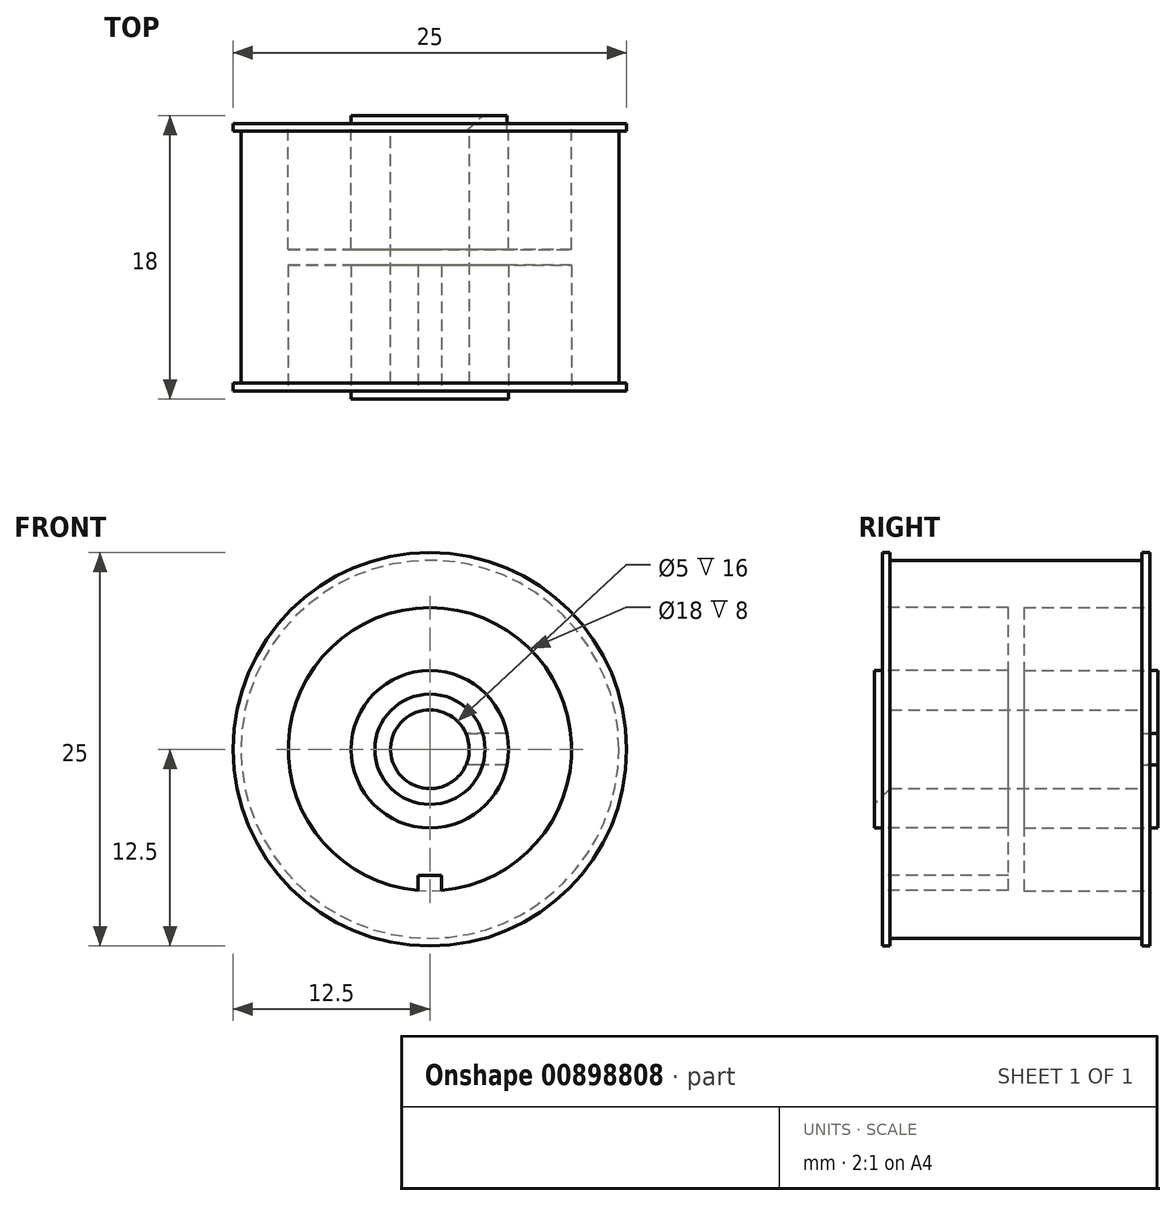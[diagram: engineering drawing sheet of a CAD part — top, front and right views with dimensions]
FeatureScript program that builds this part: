
annotation { "Feature Type Name" : "Feature", "Feature Type Description" : "" }
export const myFeature = defineFeature(function(context is Context, id is Id, definition is map)
    precondition{}
    {
        {
            var Q0;
            Q0=qCreatedBy(makeId("Front.planeOp"),FACE);
            var sketch = newSketch(context, id + "F0", { "sketchPlane" : qUnion([Q0])});
            skCircle(sketch, "E0", {"center": v(0, 0) * mm, "radius": 12.5 * mm});
            skSolve(sketch);
        }
        {
            var Q0;
            Q0 = qSketchRegion(id + "F0", true);
            extrude(context, id + "F1", {"entities" : qUnion([Q0]), "depth" : 17 * mm, "offsetDistance" : 25 * mm});
        }
        {
            var Q0;
            Q0=qCreatedBy(makeId("Top.planeOp"),FACE);
            var sketch = newSketch(context, id + "F2", { "sketchPlane" : qUnion([Q0])});
            skLineSegment(sketch, "E1.bottom", {"start": v(-13.5, -0.5) * mm, "end": v(-12, -0.5) * mm});
            skLineSegment(sketch, "E1.top", {"start": v(-13.5, -16.5) * mm, "end": v(-12, -16.5) * mm});
            skLineSegment(sketch, "E1.left", {"start": v(-13.5, -0.5) * mm, "end": v(-13.5, -16.5) * mm});
            skLineSegment(sketch, "E1.right", {"start": v(-12, -0.5) * mm, "end": v(-12, -16.5) * mm});
            skLineSegment(sketch, "E2", {"start": v(0, 0.56) * mm, "end": v(0, -16.99) * mm});
            skSolve(sketch);
        }
        {
            var Q0;
            Q0 = qSketchRegion(id + "F2", true);
            var Q1;
            Q1=sQuery(id+"F2.wireOp",EDGE,"E2");
            revolve(context, id + "F3", {"operationType" : NewBodyOperationType.REMOVE, "surfaceOperationType" : NewSurfaceOperationType.NEW, "entities" : qUnion([Q0]), "axis" : qUnion([Q1]), "revolveType" : RevolveType.FULL, "oppositeDirection" : true});
        }
        {
            var Q0;
            Q0=makeQuery(id+"F1.opExtrude","CAP_FACE",FACE,{"disambiguationData":[OSD([sQuery(id+"F0.wireOp",EDGE,"E0")])],"isStart":true});
            var sketch = newSketch(context, id + "F4", { "sketchPlane" : qUnion([Q0])});
            skCircle(sketch, "E3", {"center": v(0, 0) * mm, "radius": 2.5 * mm});
            skSolve(sketch);
        }
        {
            var Q0;
            Q0 = qSketchRegion(id + "F4", true);
            extrude(context, id + "F5", {"entities" : qUnion([Q0]), "operationType" : NewBodyOperationType.REMOVE, "endBound" : BoundingType.THROUGH_ALL, "oppositeDirection" : true, "depth" : 25 * mm, "offsetDistance" : 25 * mm});
        }
        {
            var Q0;
            Q0=makeQuery(id+"F1.opExtrude","CAP_FACE",FACE,{"disambiguationData":[OSD([sQuery(id+"F0.wireOp",EDGE,"E0")])],"isStart":true});
            var sketch = newSketch(context, id + "F6", { "sketchPlane" : qUnion([Q0])});
            skCircle(sketch, "E4", {"center": v(0, 0) * mm, "radius": 9 * mm});
            skCircle(sketch, "E5", {"center": v(0, 0) * mm, "radius": 5 * mm});
            skSolve(sketch);
        }
        {
            var Q0;
            Q0 = qSketchRegion(id + "F6", true);
            extrude(context, id + "F7", {"entities" : qUnion([Q0]), "operationType" : NewBodyOperationType.REMOVE, "oppositeDirection" : true, "depth" : 8 * mm, "offsetDistance" : 25 * mm});
        }
        {
            var Q0;
            Q0=makeQuery(id+"F7.boolean.opBoolean","SPLIT",FACE,{"disambiguationData":[TD([makeQuery(id+"F5.boolean.opBoolean","COPY",FACE,{"derivedFrom":makeQuery(id+"F5.opExtrude","SWEPT_FACE",FACE,{"disambiguationData":[OSD([sQuery(id+"F4.wireOp",EDGE,"E3")])]})})])],"derivedFrom":makeQuery(id+"F1.opExtrude","CAP_FACE",FACE,{"disambiguationData":[OSD([sQuery(id+"F0.wireOp",EDGE,"E0")])],"isStart":true})});
            var sketch = newSketch(context, id + "F8", { "sketchPlane" : qUnion([Q0])});
            skLineSegment(sketch, "E6.bottom", {"start": v(-6.33, 1) * mm, "end": v(-1.4, 1) * mm});
            skLineSegment(sketch, "E6.top", {"start": v(-6.33, -1) * mm, "end": v(-1.4, -1) * mm});
            skLineSegment(sketch, "E6.left", {"start": v(-6.33, 1) * mm, "end": v(-6.33, -1) * mm});
            skLineSegment(sketch, "E6.right", {"start": v(-1.4, 1) * mm, "end": v(-1.4, -1) * mm});
            skSolve(sketch);
        }
        {
            var Q0;
            Q0 = qSketchRegion(id + "F8", true);
            extrude(context, id + "F9", {"entities" : qUnion([Q0]), "operationType" : NewBodyOperationType.REMOVE, "oppositeDirection" : true, "depth" : .5 * mm, "offsetDistance" : 25 * mm});
        }
        {
            var Q0;
            Q0=makeQuery(id+"F1.opExtrude","CAP_FACE",FACE,{"disambiguationData":[OSD([sQuery(id+"F0.wireOp",EDGE,"E0")])],"isStart":false});
            var sketch = newSketch(context, id + "F10", { "sketchPlane" : qUnion([Q0])});
            skArc(sketch, "E7", {"start": v(0.75, -8.97) * mm, "mid": v(0, 9) * mm, "end": v(-0.75, -8.97) * mm});
            skCircle(sketch, "E8", {"center": v(0, 0) * mm, "radius": 5 * mm});
            skLineSegment(sketch, "E9.top", {"start": v(-0.75, -8) * mm, "end": v(0.75, -8) * mm});
            skLineSegment(sketch, "E9.left", {"start": v(-0.75, -8.97) * mm, "end": v(-0.75, -8) * mm});
            skLineSegment(sketch, "E9.right", {"start": v(0.75, -8.97) * mm, "end": v(0.75, -8) * mm});
            skSolve(sketch);
        }
        {
            var Q0;
            Q0 = qSketchRegion(id + "F10", true);
            extrude(context, id + "F11", {"entities" : qUnion([Q0]), "operationType" : NewBodyOperationType.REMOVE, "oppositeDirection" : true, "depth" : 8 * mm, "offsetDistance" : 25 * mm});
        }
        {
            var Q0;
            Q0=makeQuery(id+"F7.boolean.opBoolean","SPLIT",FACE,{"disambiguationData":[TD([makeQuery(id+"F5.boolean.opBoolean","COPY",FACE,{"derivedFrom":makeQuery(id+"F5.opExtrude","SWEPT_FACE",FACE,{"disambiguationData":[OSD([sQuery(id+"F4.wireOp",EDGE,"E3")])]})})])],"derivedFrom":makeQuery(id+"F1.opExtrude","CAP_FACE",FACE,{"disambiguationData":[OSD([sQuery(id+"F0.wireOp",EDGE,"E0")])],"isStart":true})});
            extrude(context, id + "F12", {"entities" : qUnion([Q0]), "operationType" : NewBodyOperationType.ADD, "depth" : .5 * mm, "offsetDistance" : 25 * mm});
        }
        {
            var Q0;
            Q0=makeQuery(id+"F11.boolean.opBoolean","SPLIT",FACE,{"disambiguationData":[TD([makeQuery(id+"F5.boolean.opBoolean","COPY",FACE,{"derivedFrom":makeQuery(id+"F5.opExtrude","SWEPT_FACE",FACE,{"disambiguationData":[OSD([sQuery(id+"F4.wireOp",EDGE,"E3")])]})})])],"derivedFrom":makeQuery(id+"F1.opExtrude","CAP_FACE",FACE,{"disambiguationData":[OSD([sQuery(id+"F0.wireOp",EDGE,"E0")])],"isStart":false})});
            extrude(context, id + "F13", {"entities" : qUnion([Q0]), "operationType" : NewBodyOperationType.ADD, "depth" : .5 * mm, "offsetDistance" : 25 * mm});
        }
        {
            var Q0;
            Q0=makeQuery(id+"F13.opExtrude","CAP_EDGE",EDGE,{"disambiguationData":[OSD([sQuery(id+"F0.wireOp",EDGE,"E0"),sQuery(id+"F4.wireOp",EDGE,"E3")])],"isStart":false});
            var Q1;
            Q1=makeQuery(id+"F12.opExtrude","CAP_EDGE",EDGE,{"disambiguationData":[OSD([sQuery(id+"F4.wireOp",EDGE,"E3")])],"isStart":false});
            chamfer(context, id + "F14", {"entities" : qUnion([Q0, Q1]), "width" : 1 * mm, "tangentPropagation" : true});
        }
    });
